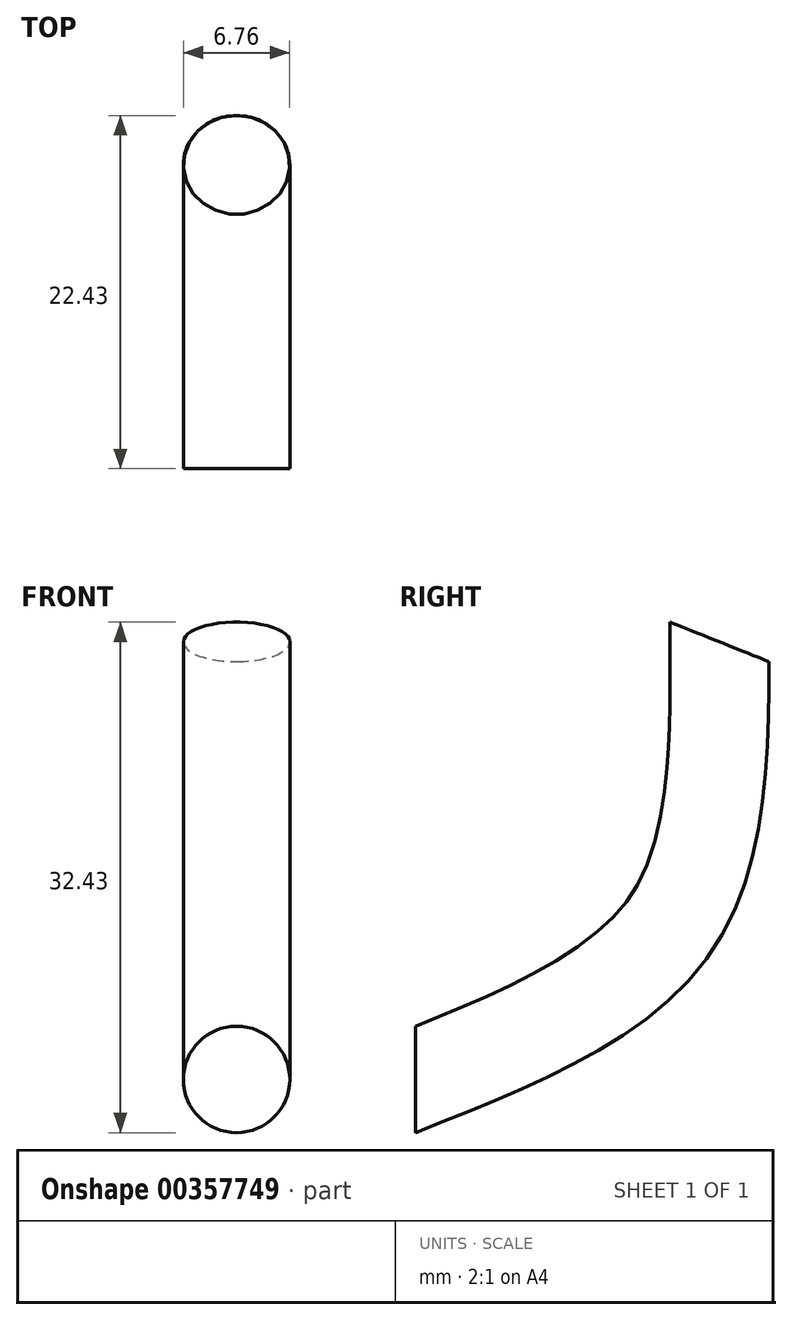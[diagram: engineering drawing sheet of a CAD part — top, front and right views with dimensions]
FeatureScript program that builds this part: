
annotation { "Feature Type Name" : "Feature", "Feature Type Description" : "" }
export const myFeature = defineFeature(function(context is Context, id is Id, definition is map)
    precondition{}
    {
        {
            var Q0;
            Q0=qCreatedBy(makeId("Right.planeOp"),FACE);
            var sketch = newSketch(context, id + "F0", { "sketchPlane" : qUnion([Q0])});
            skFitSpline(sketch, "E0", {"points": [v(0, 0) * mm, v(16.18, 9.93) * mm, v(19.29, 27.8) * mm], "startDerivative": vector(38.48, 15.47) * mm, "endDerivative": vector(-0.06, 40.22) * mm});
            skSolve(sketch);
        }
        {
            var Q0;
            Q0=qCreatedBy(makeId("Front.planeOp"),FACE);
            var sketch = newSketch(context, id + "F1", { "sketchPlane" : qUnion([Q0])});
            skCircle(sketch, "E1", {"center": v(0, 0) * mm, "radius": 3.38 * mm});
            skSolve(sketch);
        }
        {
            var Q0;
            Q0=makeQuery(id+"F1.imprint","IMPRINT",FACE,{"disambiguationData":[TD([[makeQuery(id+"F1.imprint","IMPRINT",EDGE,{"derivedFrom":sQuery(id+"F1.wireOp",EDGE,"E1")}),1.0]])]});
            var Q1;
            Q1=sQuery(id+"F0.wireOp",EDGE,"E0");
            sweep(context, id + "F2", {"profiles" : qUnion([Q0]), "path" : qUnion([Q1])});
        }
    });
